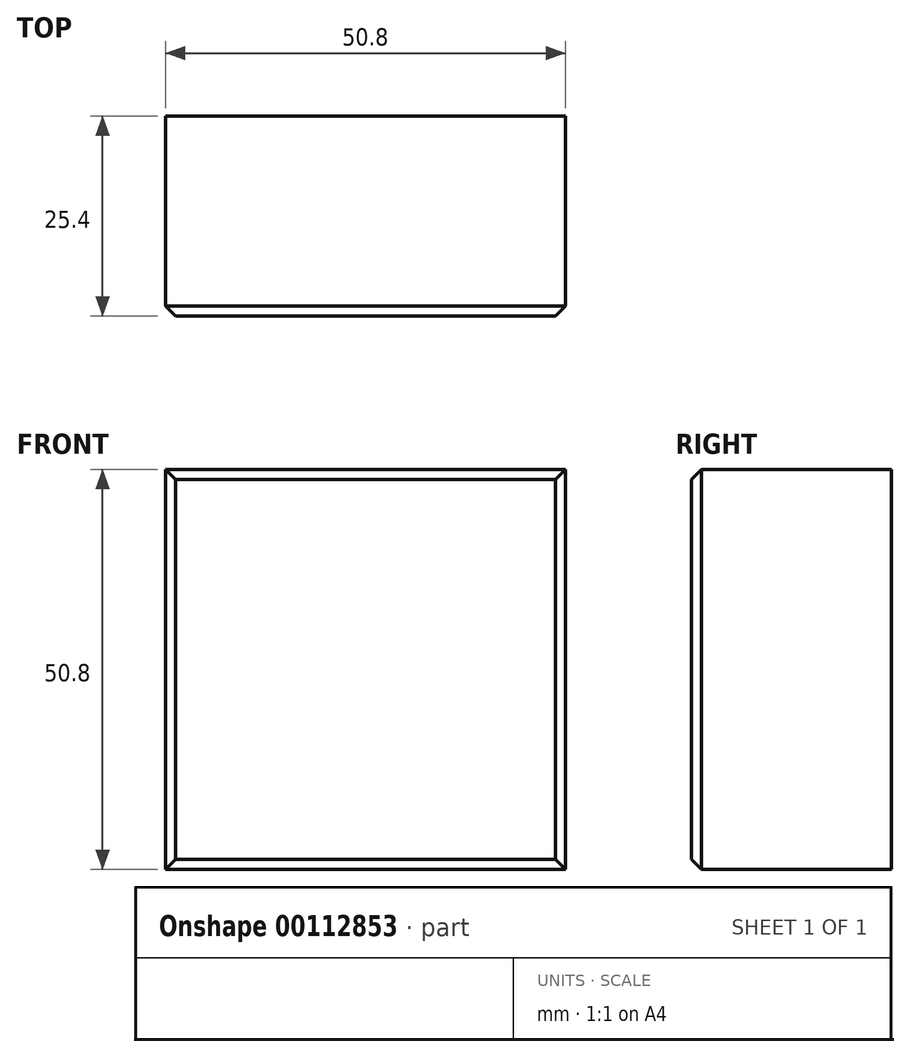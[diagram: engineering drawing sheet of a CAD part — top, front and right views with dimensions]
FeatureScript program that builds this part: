
annotation { "Feature Type Name" : "Feature", "Feature Type Description" : "" }
export const myFeature = defineFeature(function(context is Context, id is Id, definition is map)
    precondition{}
    {
        {
            var Q0;
            Q0=qCreatedBy(makeId("Front.planeOp"),FACE);
            var sketch = newSketch(context, id + "F0", { "sketchPlane" : qUnion([Q0])});
            skLineSegment(sketch, "E0.bottom", {"start": v(0, 0) * mm, "end": v(50.8, 0) * mm});
            skLineSegment(sketch, "E0.top", {"start": v(0, 50.8) * mm, "end": v(50.8, 50.8) * mm});
            skLineSegment(sketch, "E0.left", {"start": v(0, 0) * mm, "end": v(0, 50.8) * mm});
            skLineSegment(sketch, "E0.right", {"start": v(50.8, 0) * mm, "end": v(50.8, 50.8) * mm});
            skSolve(sketch);
        }
        {
            var Q0;
            Q0=makeQuery(id+"F0.imprint","IMPRINT",FACE,{"disambiguationData":[TD([[makeQuery(id+"F0.imprint","IMPRINT",EDGE,{"derivedFrom":sQuery(id+"F0.wireOp",EDGE,"E0.bottom")}),1.0]])]});
            extrude(context, id + "F1", {"entities" : qUnion([Q0]), "depth" : 25.4 * mm});
        }
        {
            var Q0;
            Q0=makeQuery(id+"F1.opExtrude","CAP_EDGE",EDGE,{"disambiguationData":[OSD([sQuery(id+"F0.wireOp",EDGE,"E0.left")])],"isStart":false});
            var Q1;
            Q1=makeQuery(id+"F1.opExtrude","CAP_EDGE",EDGE,{"disambiguationData":[OSD([sQuery(id+"F0.wireOp",EDGE,"E0.top")])],"isStart":false});
            var Q2;
            Q2=makeQuery(id+"F1.opExtrude","CAP_EDGE",EDGE,{"disambiguationData":[OSD([sQuery(id+"F0.wireOp",EDGE,"E0.bottom")])],"isStart":false});
            var Q3;
            Q3=makeQuery(id+"F1.opExtrude","CAP_EDGE",EDGE,{"disambiguationData":[OSD([sQuery(id+"F0.wireOp",EDGE,"E0.right")])],"isStart":false});
            chamfer(context, id + "F2", {"entities" : qUnion([Q0, Q1, Q2, Q3]), "width" : 1.27 * mm, "tangentPropagation" : true});
        }
    });
